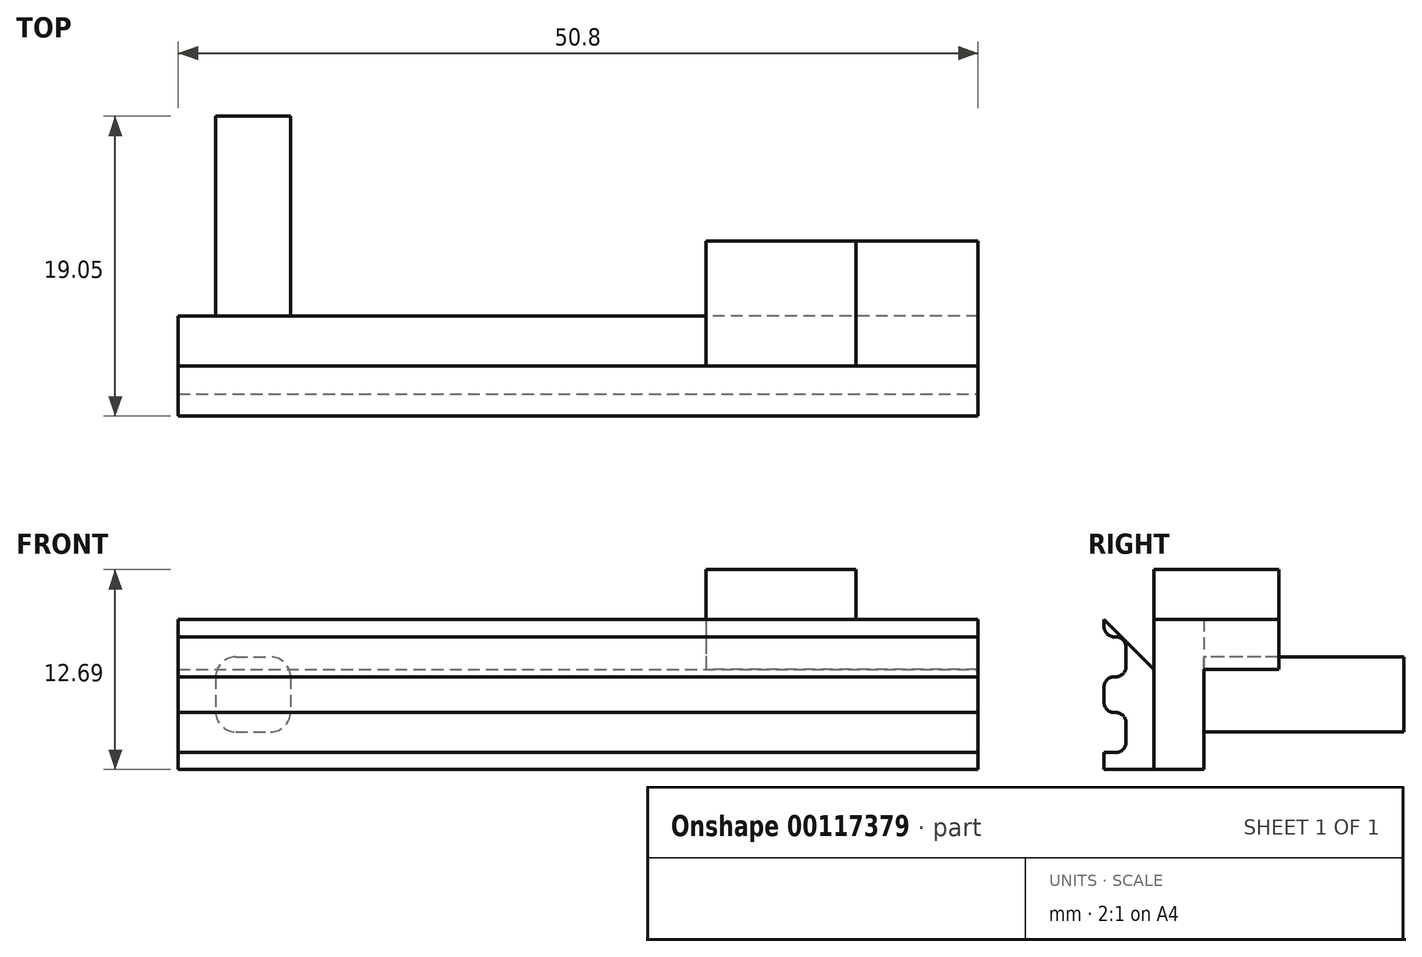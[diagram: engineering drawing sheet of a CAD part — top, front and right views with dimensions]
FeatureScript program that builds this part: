
annotation { "Feature Type Name" : "Feature", "Feature Type Description" : "" }
export const myFeature = defineFeature(function(context is Context, id is Id, definition is map)
    precondition{}
    {
        {
            var Q0;
            Q0=qCreatedBy(makeId("Front.planeOp"),FACE);
            var sketch = newSketch(context, id + "F0", { "sketchPlane" : qUnion([Q0])});
            skLineSegment(sketch, "E0.bottom", {"start": v(25.4, 4.76) * mm, "end": v(-25.4, 4.76) * mm});
            skLineSegment(sketch, "E0.top", {"start": v(25.4, -4.76) * mm, "end": v(-25.4, -4.76) * mm});
            skLineSegment(sketch, "E0.left", {"start": v(25.4, 4.76) * mm, "end": v(25.4, -4.76) * mm});
            skLineSegment(sketch, "E0.right", {"start": v(-25.4, 4.76) * mm, "end": v(-25.4, -4.76) * mm});
            skPoint(sketch, "E0.middle", {"position": v(0, 0) * mm});
            skSolve(sketch);
        }
        {
            var Q0;
            Q0=makeQuery(id+"F0.imprint","IMPRINT",FACE,{"disambiguationData":[TD([[makeQuery(id+"F0.imprint","IMPRINT",EDGE,{"derivedFrom":sQuery(id+"F0.wireOp",EDGE,"E0.bottom")}),1.0]])]});
            extrude(context, id + "F1", {"entities" : qUnion([Q0]), "depth" : 3.17 * mm});
        }
        {
            var Q0;
            Q0=makeQuery(id+"F1.opExtrude","SWEPT_FACE",FACE,{"disambiguationData":[OSD([sQuery(id+"F0.wireOp",EDGE,"E0.left")])]});
            var sketch = newSketch(context, id + "F2", { "sketchPlane" : qUnion([Q0])});
            skLineSegment(sketch, "E1", {"start": v(-3.18, -4.76) * mm, "end": v(-6.35, -4.76) * mm});
            skLineSegment(sketch, "E2.bottom", {"start": v(-3.18, 4.76) * mm, "end": v(-6.35, 4.76) * mm});
            skLineSegment(sketch, "E2.left", {"start": v(-3.18, 4.76) * mm, "end": v(-3.18, -4.76) * mm});
            skLineSegment(sketch, "E2.right", {"start": v(-6.35, 4.76) * mm, "end": v(-6.35, -4.76) * mm});
            skSolve(sketch);
        }
        {
            var Q0;
            Q0=makeQuery(id+"F2.imprint","IMPRINT",FACE,{"disambiguationData":[TD([[makeQuery(id+"F2.imprint","IMPRINT",EDGE,{"derivedFrom":sQuery(id+"F2.wireOp",EDGE,"E2.bottom")}),1.0]])]});
            extrude(context, id + "F3", {"entities" : qUnion([Q0]), "oppositeDirection" : true, "depth" : 50.8 * mm});
        }
        {
            var Q0;
            Q0=makeQuery(id+"F1.opExtrude","CAP_FACE",FACE,{"disambiguationData":[OSD([sQuery(id+"F0.wireOp",EDGE,"E0.bottom"),sQuery(id+"F0.wireOp",EDGE,"E0.top"),sQuery(id+"F0.wireOp",EDGE,"E0.left"),sQuery(id+"F0.wireOp",EDGE,"E0.right")])],"isStart":true});
            var sketch = newSketch(context, id + "F4", { "sketchPlane" : qUnion([Q0])});
            skLineSegment(sketch, "E3.bottom", {"start": v(25.4, 4.76) * mm, "end": v(15.88, 4.76) * mm});
            skLineSegment(sketch, "E3.top", {"start": v(25.4, -4.76) * mm, "end": v(15.88, -4.76) * mm});
            skLineSegment(sketch, "E3.left", {"start": v(25.4, 4.76) * mm, "end": v(25.4, -4.76) * mm});
            skLineSegment(sketch, "E3.right", {"start": v(15.88, 4.76) * mm, "end": v(15.88, -4.76) * mm});
            skLineSegment(sketch, "E4.bottom", {"start": v(23.02, 2.38) * mm, "end": v(18.26, 2.38) * mm});
            skLineSegment(sketch, "E4.top", {"start": v(23.02, -2.38) * mm, "end": v(18.26, -2.38) * mm});
            skLineSegment(sketch, "E4.left", {"start": v(23.02, 2.38) * mm, "end": v(23.02, -2.38) * mm});
            skLineSegment(sketch, "E4.right", {"start": v(18.26, 2.38) * mm, "end": v(18.26, -2.38) * mm});
            skPoint(sketch, "E4.middle", {"position": v(20.64, 0) * mm});
            skSolve(sketch);
        }
        {
            var Q0;
            Q0=makeQuery(id+"F4.imprint","IMPRINT",FACE,{"disambiguationData":[TD([[makeQuery(id+"F4.imprint","IMPRINT",EDGE,{"derivedFrom":sQuery(id+"F4.wireOp",EDGE,"E4.bottom")}),1.0]])]});
            extrude(context, id + "F5", {"entities" : qUnion([Q0]), "operationType" : NewBodyOperationType.ADD, "depth" : 12.7 * mm});
        }
        {
            var Q0;
            Q0=makeQuery(id+"F5.opExtrude","SWEPT_EDGE",EDGE,{"disambiguationData":[OSD([sQuery(id+"F4.wireOp",EDGE,"E4.bottom"),sQuery(id+"F4.wireOp",EDGE,"E4.right")])]});
            var Q1;
            Q1=makeQuery(id+"F5.opExtrude","SWEPT_EDGE",EDGE,{"disambiguationData":[OSD([sQuery(id+"F4.wireOp",EDGE,"E4.bottom"),sQuery(id+"F4.wireOp",EDGE,"E4.left")])]});
            var Q2;
            Q2=makeQuery(id+"F5.opExtrude","SWEPT_EDGE",EDGE,{"disambiguationData":[OSD([sQuery(id+"F4.wireOp",EDGE,"E4.top"),sQuery(id+"F4.wireOp",EDGE,"E4.right")])]});
            var Q3;
            Q3=makeQuery(id+"F5.opExtrude","SWEPT_EDGE",EDGE,{"disambiguationData":[OSD([sQuery(id+"F4.wireOp",EDGE,"E4.top"),sQuery(id+"F4.wireOp",EDGE,"E4.left")])]});
            fillet(context, id + "F6", {"entities" : qUnion([Q0, Q1, Q2, Q3]), "radius" : 1.27 * mm, "tangentPropagation" : true, "allowEdgeOverflow" : false});
        }
        {
            var Q0;
            Q0=makeQuery(id+"F1.opExtrude","SWEPT_FACE",FACE,{"disambiguationData":[OSD([sQuery(id+"F0.wireOp",EDGE,"E0.bottom")])]});
            var sketch = newSketch(context, id + "F7", { "sketchPlane" : qUnion([Q0])});
            skLineSegment(sketch, "E5.bottom", {"start": v(17.65, 0) * mm, "end": v(8.13, 0) * mm});
            skLineSegment(sketch, "E5.top", {"start": v(17.65, -3.18) * mm, "end": v(8.13, -3.18) * mm});
            skLineSegment(sketch, "E5.left", {"start": v(17.65, 0) * mm, "end": v(17.65, -3.17) * mm});
            skLineSegment(sketch, "E5.right", {"start": v(8.13, 0) * mm, "end": v(8.13, -3.18) * mm});
            skSolve(sketch);
        }
        {
            var Q0;
            Q0=makeQuery(id+"F7.imprint","IMPRINT",FACE,{"disambiguationData":[TD([[makeQuery(id+"F7.imprint","IMPRINT",EDGE,{"derivedFrom":sQuery(id+"F7.wireOp",EDGE,"E5.bottom")}),1.0]])]});
            extrude(context, id + "F8", {"entities" : qUnion([Q0]), "operationType" : NewBodyOperationType.ADD, "depth" : 3.17 * mm});
        }
        {
            var Q0;
            Q0=makeQuery(id+"F8.boolean.opBoolean","MERGE",FACE,{"derivedFrom":[makeQuery(id+"F1.opExtrude","CAP_FACE",FACE,{"disambiguationData":[OSD([sQuery(id+"F0.wireOp",EDGE,"E0.bottom"),sQuery(id+"F0.wireOp",EDGE,"E0.top"),sQuery(id+"F0.wireOp",EDGE,"E0.left"),sQuery(id+"F0.wireOp",EDGE,"E0.right")])],"isStart":true}),makeQuery(id+"F8.opExtrude","SWEPT_FACE",FACE,{"disambiguationData":[OSD([sQuery(id+"F7.wireOp",EDGE,"E5.bottom")])]})]});
            var sketch = newSketch(context, id + "F9", { "sketchPlane" : qUnion([Q0])});
            skLineSegment(sketch, "E6.bottom", {"start": v(-25.4, 4.76) * mm, "end": v(-8.13, 4.76) * mm});
            skLineSegment(sketch, "E6.top", {"start": v(-25.4, 1.59) * mm, "end": v(-8.13, 1.59) * mm});
            skLineSegment(sketch, "E6.left", {"start": v(-25.4, 4.76) * mm, "end": v(-25.4, 1.59) * mm});
            skLineSegment(sketch, "E6.right", {"start": v(-8.13, 4.76) * mm, "end": v(-8.13, 1.59) * mm});
            skSolve(sketch);
        }
        {
            var Q0;
            Q0 = qSketchRegion(id + "F9", true);
            var Q1;
            {var subQ1=sQuery(id+"F7.wireOp",EDGE,"E5.bottom");Q1=makeQuery(id+"F9.imprint","IMPRINT",FACE,{"disambiguationData":[TD([[makeQuery(id+"F9.imprint","IMPRINT",EDGE,{"derivedFrom":makeQuery(id+"F8.opExtrude","CAP_EDGE",EDGE,{"disambiguationData":[OSD([subQ1])],"isStart":false})}),-1.0]])]});}
            extrude(context, id + "F10", {"entities" : qUnion([Q0, Q1]), "operationType" : NewBodyOperationType.ADD, "depth" : 4.76 * mm});
        }
        {
            var Q0;
            Q0=makeQuery(id+"F3.opExtrude","CAP_FACE",FACE,{"disambiguationData":[OSD([sQuery(id+"F2.wireOp",EDGE,"E2.bottom"),sQuery(id+"F2.wireOp",EDGE,"E1"),sQuery(id+"F2.wireOp",EDGE,"E2.left"),sQuery(id+"F2.wireOp",EDGE,"E2.right")])],"isStart":true});
            var sketch = newSketch(context, id + "F11", { "sketchPlane" : qUnion([Q0])});
            skLineSegment(sketch, "E7.bottom", {"start": v(-6.35, -3.69) * mm, "end": v(-4.96, -3.69) * mm});
            skLineSegment(sketch, "E7.top", {"start": v(-6.35, -1.15) * mm, "end": v(-4.96, -1.15) * mm});
            skLineSegment(sketch, "E7.left", {"start": v(-6.35, -3.69) * mm, "end": v(-6.35, -1.15) * mm});
            skLineSegment(sketch, "E7.right", {"start": v(-4.96, -3.69) * mm, "end": v(-4.96, -1.15) * mm});
            skLineSegment(sketch, "E8.bottom", {"start": v(-6.35, 3.66) * mm, "end": v(-4.96, 3.66) * mm});
            skLineSegment(sketch, "E8.top", {"start": v(-6.35, 1.12) * mm, "end": v(-4.96, 1.12) * mm});
            skLineSegment(sketch, "E8.left", {"start": v(-6.35, 3.66) * mm, "end": v(-6.35, 1.12) * mm});
            skLineSegment(sketch, "E8.right", {"start": v(-4.96, 3.66) * mm, "end": v(-4.96, 1.12) * mm});
            skSolve(sketch);
        }
        {
            var Q0;
            Q0=makeQuery(id+"F11.imprint","IMPRINT",FACE,{"disambiguationData":[TD([[makeQuery(id+"F11.imprint","IMPRINT",EDGE,{"derivedFrom":sQuery(id+"F11.wireOp",EDGE,"E8.bottom")}),-1.0]])]});
            var Q1;
            Q1=makeQuery(id+"F11.imprint","IMPRINT",FACE,{"disambiguationData":[TD([[makeQuery(id+"F11.imprint","IMPRINT",EDGE,{"derivedFrom":sQuery(id+"F11.wireOp",EDGE,"E7.bottom")}),1.0]])]});
            extrude(context, id + "F12", {"entities" : qUnion([Q0, Q1]), "operationType" : NewBodyOperationType.REMOVE, "oppositeDirection" : true, "depth" : 50.8 * mm});
        }
        {
            var Q0;
            Q0=makeQuery(id+"F12.boolean.opBoolean","COPY",EDGE,{"derivedFrom":makeQuery(id+"F12.opExtrude","SWEPT_EDGE",EDGE,{"disambiguationData":[OSD([sQuery(id+"F11.wireOp",EDGE,"E8.top"),sQuery(id+"F11.wireOp",EDGE,"E8.right")])]})});
            var Q1;
            Q1=makeQuery(id+"F12.boolean.opBoolean","COPY",EDGE,{"derivedFrom":makeQuery(id+"F12.opExtrude","SWEPT_EDGE",EDGE,{"disambiguationData":[OSD([sQuery(id+"F11.wireOp",EDGE,"E8.bottom"),sQuery(id+"F11.wireOp",EDGE,"E8.right")])]})});
            var Q2;
            Q2=makeQuery(id+"F12.boolean.opBoolean","COPY",EDGE,{"derivedFrom":makeQuery(id+"F12.opExtrude","SWEPT_EDGE",EDGE,{"disambiguationData":[OSD([sQuery(id+"F11.wireOp",EDGE,"E7.bottom"),sQuery(id+"F11.wireOp",EDGE,"E7.right")])]})});
            var Q3;
            Q3=makeQuery(id+"F12.boolean.opBoolean","COPY",EDGE,{"derivedFrom":makeQuery(id+"F12.opExtrude","SWEPT_EDGE",EDGE,{"disambiguationData":[OSD([sQuery(id+"F11.wireOp",EDGE,"E7.top"),sQuery(id+"F11.wireOp",EDGE,"E7.right")])]})});
            var Q4;
            Q4=makeQuery(id+"F12.boolean.opBoolean","COPY",EDGE,{"derivedFrom":makeQuery(id+"F12.opExtrude","SWEPT_EDGE",EDGE,{"disambiguationData":[OSD([sQuery(id+"F2.wireOp",EDGE,"E2.right"),sQuery(id+"F11.wireOp",EDGE,"E8.top"),sQuery(id+"F11.wireOp",EDGE,"E8.left")])]})});
            var Q5;
            Q5=makeQuery(id+"F12.boolean.opBoolean","COPY",EDGE,{"derivedFrom":makeQuery(id+"F12.opExtrude","SWEPT_EDGE",EDGE,{"disambiguationData":[OSD([sQuery(id+"F2.wireOp",EDGE,"E2.right"),sQuery(id+"F11.wireOp",EDGE,"E7.top"),sQuery(id+"F11.wireOp",EDGE,"E7.left")])]})});
            var Q6;
            Q6=makeQuery(id+"F12.boolean.opBoolean","COPY",EDGE,{"derivedFrom":makeQuery(id+"F12.opExtrude","SWEPT_EDGE",EDGE,{"disambiguationData":[OSD([sQuery(id+"F2.wireOp",EDGE,"E2.right"),sQuery(id+"F11.wireOp",EDGE,"E8.bottom"),sQuery(id+"F11.wireOp",EDGE,"E8.left")])]})});
            var Q7;
            Q7=makeQuery(id+"F12.boolean.opBoolean","COPY",EDGE,{"derivedFrom":makeQuery(id+"F12.opExtrude","SWEPT_EDGE",EDGE,{"disambiguationData":[OSD([sQuery(id+"F2.wireOp",EDGE,"E2.right"),sQuery(id+"F11.wireOp",EDGE,"E7.bottom"),sQuery(id+"F11.wireOp",EDGE,"E7.left")])]})});
            fillet(context, id + "F13", {"entities" : qUnion([Q0, Q1, Q2, Q3, Q4, Q5, Q6, Q7]), "radius" : 0.64 * mm, "tangentPropagation" : true, "allowEdgeOverflow" : false});
        }
        {
            var Q0;
            Q0=makeQuery(id+"F3.opExtrude","SWEPT_EDGE",EDGE,{"disambiguationData":[OSD([sQuery(id+"F0.wireOp",EDGE,"E0.bottom"),sQuery(id+"F0.wireOp",EDGE,"E0.left"),sQuery(id+"F2.wireOp",EDGE,"E2.bottom"),sQuery(id+"F2.wireOp",EDGE,"E2.left")])]});
            chamfer(context, id + "F14", {"entities" : qUnion([Q0]), "width" : 3.17 * mm, "tangentPropagation" : true});
        }
    });
